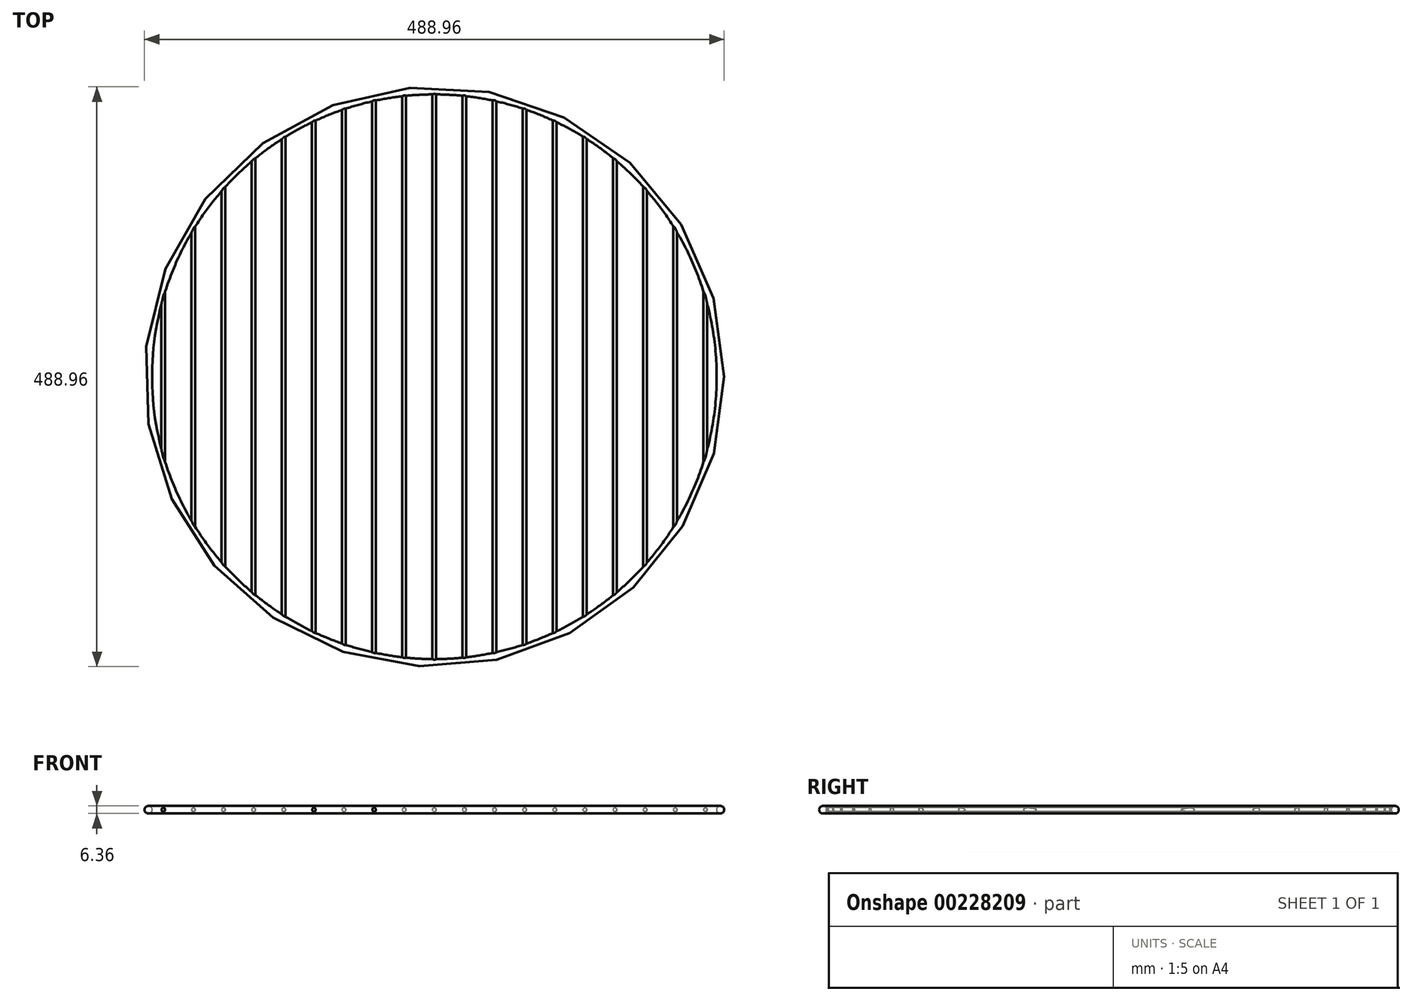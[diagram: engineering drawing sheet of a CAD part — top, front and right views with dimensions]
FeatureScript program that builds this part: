
annotation { "Feature Type Name" : "Feature", "Feature Type Description" : "" }
export const myFeature = defineFeature(function(context is Context, id is Id, definition is map)
    precondition{}
    {
        {
            var Q0;
            Q0=qCreatedBy(makeId("Front.planeOp"),FACE);
            var sketch = newSketch(context, id + "F0", { "sketchPlane" : qUnion([Q0])});
            skCircle(sketch, "E0", {"center": v(241.3, 0) * mm, "radius": 3.18 * mm});
            skLineSegment(sketch, "E1", {"start": v(0, 0) * mm, "end": v(0, 32.12) * mm, "construction": true});
            skSolve(sketch);
        }
        {
            var Q0;
            Q0=qCreatedBy(makeId("Front.planeOp"),FACE);
            var sketch = newSketch(context, id + "F1", { "sketchPlane" : qUnion([Q0])});
            skCircle(sketch, "E2", {"center": v(0, 0) * mm, "radius": 1.59 * mm});
            skCircle(sketch, "E3.1.0.0", {"center": v(-25.4, 0) * mm, "radius": 1.59 * mm});
            skCircle(sketch, "E3.2.0.0", {"center": v(-50.8, 0) * mm, "radius": 1.59 * mm});
            skCircle(sketch, "E3.3.0.0", {"center": v(-76.2, 0) * mm, "radius": 1.59 * mm});
            skCircle(sketch, "E3.4.0.0", {"center": v(-101.6, 0) * mm, "radius": 1.59 * mm});
            skLineSegment(sketch, "E3.direction1", {"start": v(0, 0) * mm, "end": v(-25.4, 0) * mm, "construction": true});
            skCircle(sketch, "E4.0.5.0", {"center": v(-127, 0) * mm, "radius": 1.59 * mm});
            skCircle(sketch, "E4.0.6.0", {"center": v(-152.4, 0) * mm, "radius": 1.59 * mm});
            skCircle(sketch, "E4.0.7.0", {"center": v(-177.8, 0) * mm, "radius": 1.59 * mm});
            skCircle(sketch, "E4.0.8.0", {"center": v(-203.2, 0) * mm, "radius": 1.59 * mm});
            skCircle(sketch, "E4.0.9.0", {"center": v(-228.6, 0) * mm, "radius": 1.59 * mm});
            skCircle(sketch, "E5.1.0.0", {"center": v(25.4, 0) * mm, "radius": 1.59 * mm});
            skCircle(sketch, "E5.2.0.0", {"center": v(50.8, 0) * mm, "radius": 1.59 * mm});
            skCircle(sketch, "E5.3.0.0", {"center": v(76.2, 0) * mm, "radius": 1.59 * mm});
            skCircle(sketch, "E5.4.0.0", {"center": v(101.6, 0) * mm, "radius": 1.59 * mm});
            skCircle(sketch, "E5.5.0.0", {"center": v(127, 0) * mm, "radius": 1.59 * mm});
            skCircle(sketch, "E5.6.0.0", {"center": v(152.4, 0) * mm, "radius": 1.59 * mm});
            skCircle(sketch, "E5.7.0.0", {"center": v(177.8, 0) * mm, "radius": 1.59 * mm});
            skCircle(sketch, "E5.8.0.0", {"center": v(203.2, 0) * mm, "radius": 1.59 * mm});
            skCircle(sketch, "E5.9.0.0", {"center": v(228.6, 0) * mm, "radius": 1.59 * mm});
            skLineSegment(sketch, "E5.direction1", {"start": v(0, 0) * mm, "end": v(25.4, 0) * mm, "construction": true});
            skSolve(sketch);
        }
        {
            var Q0;
            Q0=makeQuery(id+"F0.imprint","IMPRINT",FACE,{"disambiguationData":[TD([[makeQuery(id+"F0.imprint","IMPRINT",EDGE,{"derivedFrom":sQuery(id+"F0.wireOp",EDGE,"E0")}),1.0]])]});
            var Q1;
            Q1=sQuery(id+"F0.wireOp",EDGE,"E1");
            revolve(context, id + "F2", {"entities" : qUnion([Q0]), "axis" : qUnion([Q1]), "revolveType" : RevolveType.FULL});
        }
        {
            var Q0;
            Q0 = qSketchRegion(id + "F1", true);
            extrude(context, id + "F3", {"entities" : qUnion([Q0]), "operationType" : NewBodyOperationType.ADD, "endBound" : BoundingType.UP_TO_NEXT, "oppositeDirection" : true, "depth" : 25.4 * mm, "hasSecondDirection" : true, "secondDirectionBound" : SecondDirectionBoundingType.UP_TO_NEXT, "secondDirectionOppositeDirection" : false, "secondDirectionDepth" : 25.4 * mm});
        }
    });
